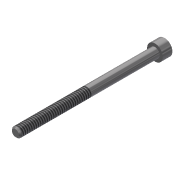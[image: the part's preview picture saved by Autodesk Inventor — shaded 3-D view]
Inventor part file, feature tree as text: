
AUTODESK INVENTOR PART (.ipt)
format: ipt  version: 2013 (Build 170138000, 138)  size: 99,840 bytes
history: native  units: in
note: dims shown in document units (in); Inventor stores cm internally (conversion verified against a paired STEP export)
features: extrude x3, sketch x3, chamfer x1, thread x1
ambient origin geometry x8: Origin, YZ Plane, XZ Plane, XY Plane, X Axis, Y Axis, Z Axis, Center Point
bodies: Solid1 (feature_tree)
feature tree (8):
  extrude  "Extrusion1"  Depth=2.0in TaperAngle=0.0deg
  extrude  "Extrusion2"  Depth=0.138in TaperAngle=0.0deg
  extrude  "Extrusion3"  Depth=0.069in TaperAngle=0.0deg
  chamfer  "Chamfer1"  Distance=0.02in Angle=45.0deg
  thread  "Thread2"  [1 undecoded]
  sketch  "Sketch1"  dims[d0=0.138in d1=2.0in d2=0.0in]
  sketch  "Sketch2"  dims[d3=0.226in d4=0.138in d5=0.0in]
  sketch  "Sketch3"  dims[d6=0.1094in d7=0.069in d8=0.0in d11=0.02in d12=0.125in d13=45.0deg d14=1.0in d15=0.0in]
note: 1 required parameter value undecoded (feature->parameter linkage not recoverable at this tier; creation-order binding heuristic only, values carry confidence <= 0.55)
